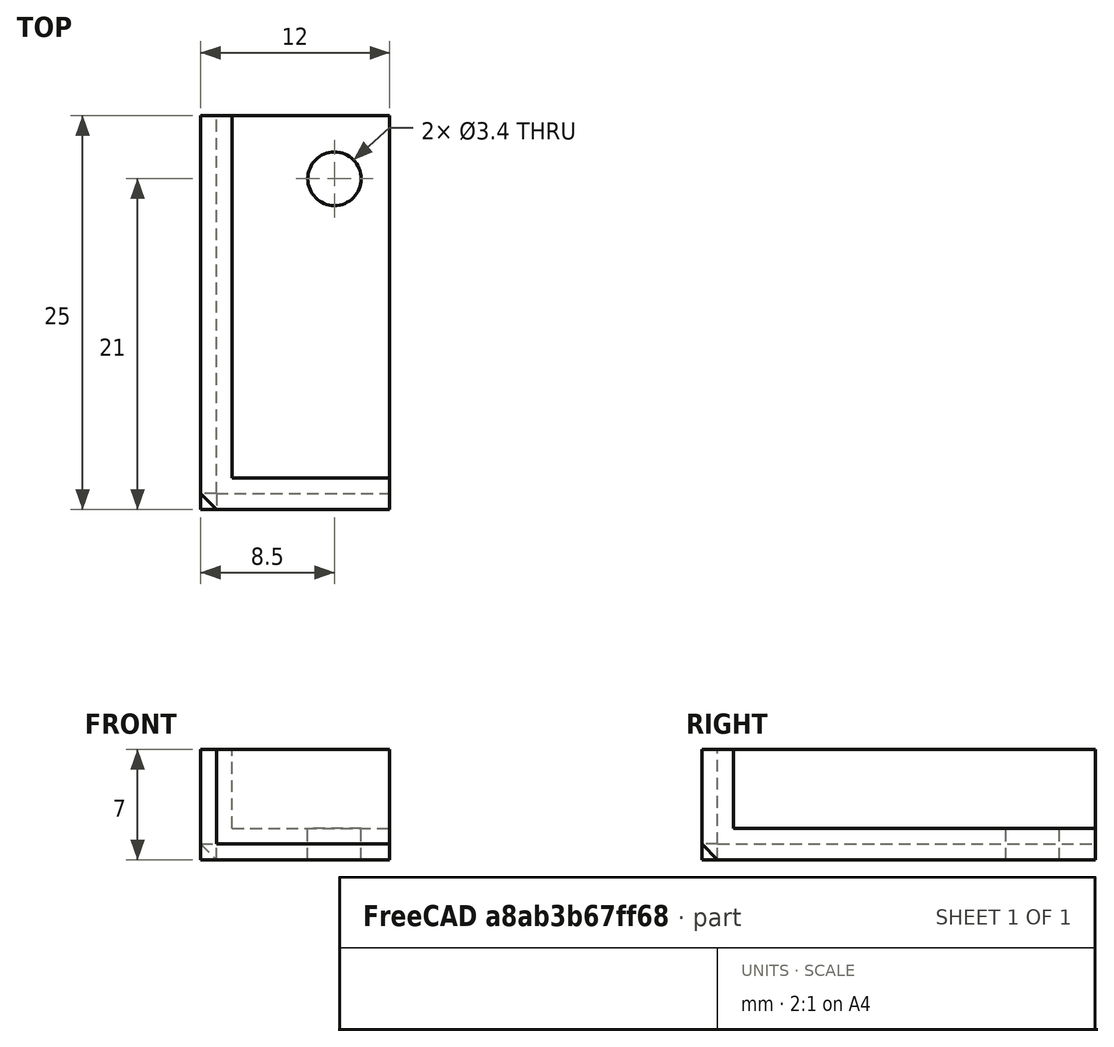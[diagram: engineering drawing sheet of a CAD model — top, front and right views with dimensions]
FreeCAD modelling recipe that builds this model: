
FCSTD DOCUMENT  (FreeCAD 0.18R16146 (Git))
Label: bed-drill-pos
License: All rights reserved
LicenseURL: http://en.wikipedia.org/wiki/All_rights_reserved
objects: Part::Box×3, Part::Cylinder×1, Part::Cut×1, Part::MultiFuse×1, Part::Feature×1, Part::Chamfer×1
note: 8 computed .brp shape members not serialized (recipe doc carries the construction recipe); baked Part::Feature solids carry a one-line shape summary decoded from their .brp

FEATURE [Part::Cylinder] Cylinder
  Angle = 360
  AttacherType = Attacher::AttachEngine3D
  Height = 10
  Placement = pos=(6.5,19,0) rot=(0,0,1;0rad)
  Radius = 1.7
FEATURE [Part::Box] Box  label="Cube"
  AttacherType = Attacher::AttachEngine3D
  Height = 7
  Length = 10
  Placement = pos=(0,-2,0) rot=(0,0,1;0rad)
  Width = 2
FEATURE [Part::Box] Box001  label="Cube001"
  AttacherType = Attacher::AttachEngine3D
  Height = 7
  Length = 2
  Placement = pos=(-2,-2,0) rot=(0,0,1;0rad)
  Width = 25
FEATURE [Part::Box] Box002  label="Cube002"
  AttacherType = Attacher::AttachEngine3D
  Height = 2
  Length = 12
  Placement = pos=(-2,-2,0) rot=(0,0,1;0rad)
  Width = 25
FEATURE [Part::Cut] Cut
  Base = -> Box002
  Tool = -> Cylinder
FEATURE [Part::MultiFuse] Fusion
  Shapes = -> [Cut,Box001,Box]
FEATURE [Part::Feature] Fusion001
  shape: bbox 12 x 25 x 7 mm, 10 faces (baked)
FEATURE [Part::Chamfer] Chamfer
  Base = -> Fusion001
  Edges = 3 edges r=1: [Edge1,Edge4,Edge5]
